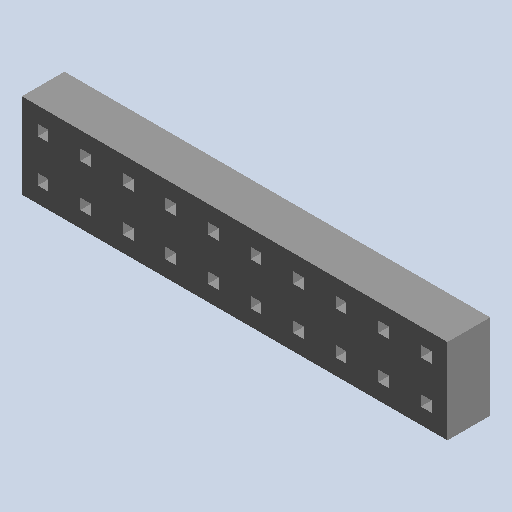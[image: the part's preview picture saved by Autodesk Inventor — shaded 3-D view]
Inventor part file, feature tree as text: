
AUTODESK INVENTOR PART (.ipt)
format: ipt  version: 2024.2 (Build 282272000, 272)  size: 176,640 bytes
history: native  units: mm (DEFAULTED — no unit token found)
features: other x7, extrude x1
ambient origin geometry x8: Origin, YZ Plane, XZ Plane, XY Plane, X Axis, Y Axis, Z Axis, Center Point
bodies: Solid1 (feature_tree)
feature tree (8):
  extrude  "Extrusion1"  Depth=2.0066mm TaperAngle=0.0deg
  other  "0_XY"
  other  "0_YZ"
  other  "0_ZX"
  other  "0_X"
  other  "0_Y"
  other  "0_Z"
  other  "0_Center"
